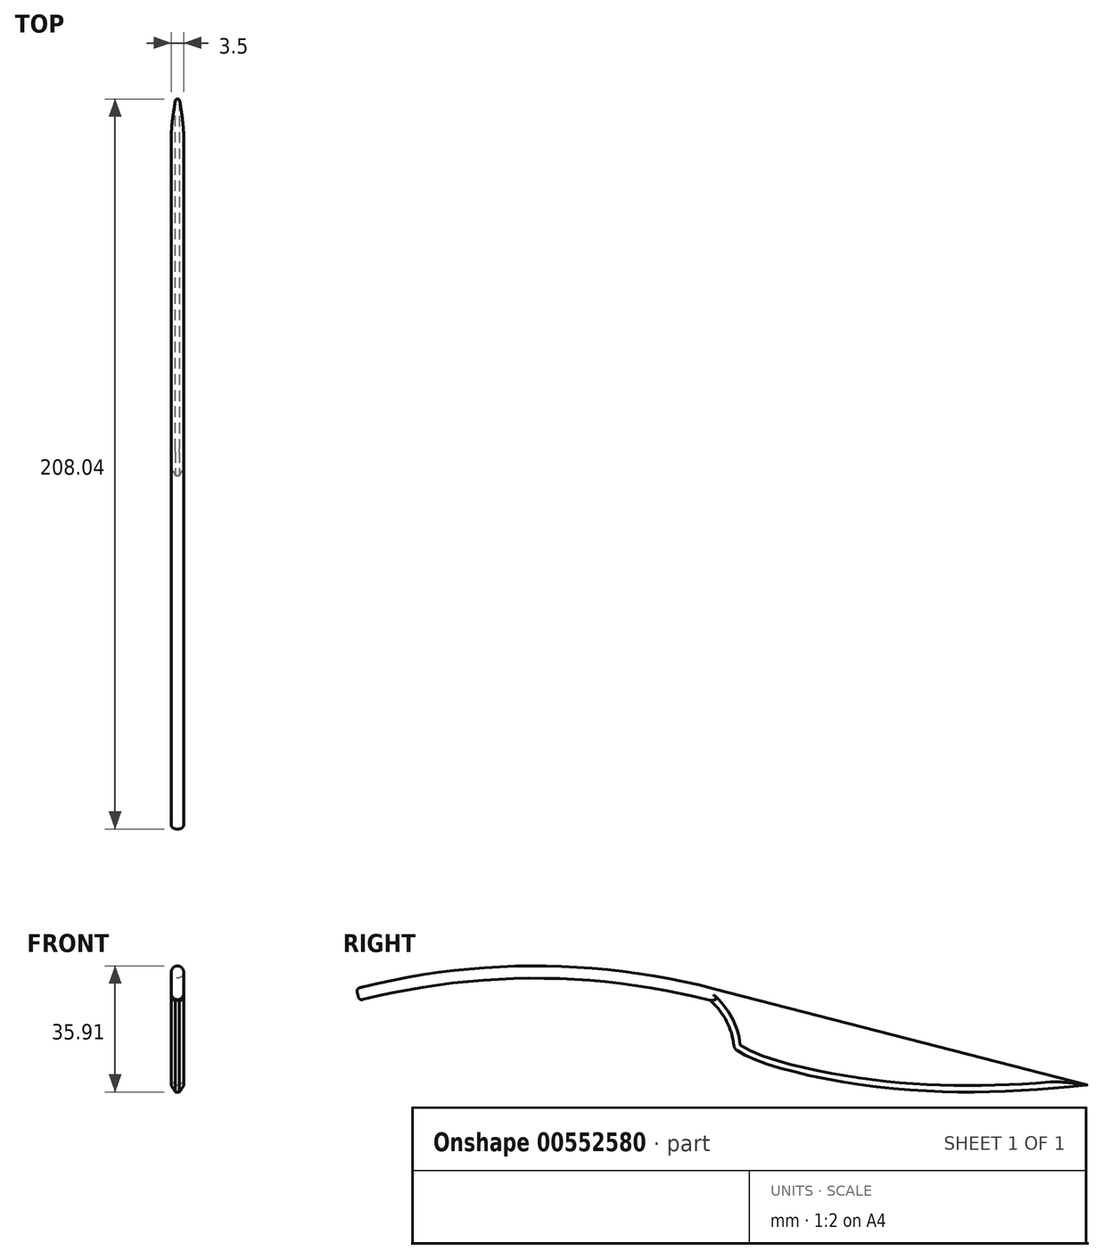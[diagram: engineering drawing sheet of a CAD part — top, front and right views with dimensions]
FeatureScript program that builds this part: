
annotation { "Feature Type Name" : "Feature", "Feature Type Description" : "" }
export const myFeature = defineFeature(function(context is Context, id is Id, definition is map)
    precondition{}
    {
        {
            var Q0;
            Q0=qCreatedBy(makeId("Right.planeOp"),FACE);
            var sketch = newSketch(context, id + "F0", { "sketchPlane" : qUnion([Q0])});
            skLineSegment(sketch, "E0", {"start": v(0, 0) * mm, "end": v(-100, 0) * mm, "construction": true});
            skArc(sketch, "E1", {"start": v(0, 0) * mm, "mid": v(-50, 6.35) * mm, "end": v(-100, 0) * mm, "construction": true});
            skArc(sketch, "E2.0", {"start": v(0.88, 3.39) * mm, "mid": v(-50, 9.85) * mm, "end": v(-100.88, 3.39) * mm, "construction": true});
            skArc(sketch, "E3.0", {"start": v(0.44, 1.7) * mm, "mid": v(-50, 8.1) * mm, "end": v(-100.44, 1.7) * mm});
            skLineSegment(sketch, "E4", {"start": v(-100, 0) * mm, "end": v(-100.88, 3.39) * mm, "construction": true});
            skLineSegment(sketch, "E5", {"start": v(0.88, 3.39) * mm, "end": v(107.38, -24.11) * mm});
            skLineSegment(sketch, "E6", {"start": v(0, 0) * mm, "end": v(106.5, -27.5) * mm, "construction": true});
            skLineSegment(sketch, "E7", {"start": v(0.88, 3.39) * mm, "end": v(0, 0) * mm});
            skLineSegment(sketch, "E8", {"start": v(54.13, -10.36) * mm, "end": v(50.38, -24.88) * mm, "construction": true});
            skLineSegment(sketch, "E9", {"start": v(0, 0) * mm, "end": v(118.47, 0) * mm, "construction": true});
            skArc(sketch, "E10", {"start": v(6.73, -12.78) * mm, "mid": v(4.56, -5.76) * mm, "end": v(0, 0) * mm});
            skLineSegment(sketch, "E11", {"start": v(50.38, -24.88) * mm, "end": v(1.97, -12.38) * mm, "construction": true});
            skFitSpline(sketch, "E12", {"points": [v(6.8, -13.63) * mm, v(50.38, -24.88) * mm, v(107.38, -24.11) * mm], "startDerivative": vector(40.37, -31.88) * mm, "endDerivative": vector(112.17, 10.51) * mm});
            skArc(sketch, "E13.filletArc", {"start": v(6.73, -12.78) * mm, "mid": v(7, -13.59) * mm, "end": v(7.6, -14.2) * mm});
            skPoint(sketch, "E14", {"position": v(26.17, -18.63) * mm});
            skLineSegment(sketch, "E15", {"start": v(0.44, 1.7) * mm, "end": v(97.34, -23.33) * mm});
            skLineSegment(sketch, "E16", {"start": v(97.78, -21.63) * mm, "end": v(96.9, -25.02) * mm, "construction": true});
            skPoint(sketch, "E17", {"position": v(97.34, -23.33) * mm});
            skLineSegment(sketch, "E18", {"start": v(97.34, -23.33) * mm, "end": v(97.78, -21.63) * mm});
            skSolve(sketch);
        }
        {
            var Q0;
            Q0=sQuery(id+"F0.wireOp",EDGE,"E4");
            cPlane(context, id + "F1", {"entities" : qUnion([Q0]), "cplaneType" : CPlaneType.LINE_ANGLE, "offset" : 25 * mm, "angle" : 90 * degree, "width" : 150 * mm, "height" : 150 * mm});
        }
        {
            var Q0;
            Q0=qCreatedBy(id+"F1.planeOp",FACE);
            var sketch = newSketch(context, id + "F2", { "sketchPlane" : qUnion([Q0])});
            skCircle(sketch, "E19", {"center": v(0, 26.75) * mm, "radius": 1.75 * mm});
            skSolve(sketch);
        }
        {
            var Q0;
            Q0=makeQuery(id+"F2.imprint","IMPRINT",FACE,{"disambiguationData":[TD([[makeQuery(id+"F2.imprint","IMPRINT",EDGE,{"derivedFrom":sQuery(id+"F2.wireOp",EDGE,"E19")}),1.0]])]});
            var Q1;
            Q1=sQuery(id+"F0.wireOp",EDGE,"E15");
            var Q2;
            Q2=sQuery(id+"F0.wireOp",EDGE,"E3.0");
            sweep(context, id + "F3", {"profiles" : qUnion([Q0]), "path" : qUnion([Q1, Q2])});
        }
        {
            var Q0;
            {var subQ3=sQuery(id+"F0.wireOp",EDGE,"E10");Q0=makeQuery(id+"F0.imprint","IMPRINT",FACE,{"disambiguationData":[TD([[makeQuery(id+"F0.imprint","IMPRINT",EDGE,{"derivedFrom":subQ3}),-1.0]])]});}
            extrude(context, id + "F4", {"entities" : qUnion([Q0]), "operationType" : NewBodyOperationType.ADD, "depth" : 3.5 * mm, "offsetDistance" : 25 * mm, "symmetric" : true});
        }
        {
            var Q0;
            Q0=makeQuery(id+"F4.opExtrude","CAP_EDGE",EDGE,{"disambiguationData":[OSD([sQuery(id+"F0.wireOp",EDGE,"E12")])],"isStart":false});
            var Q1;
            Q1=makeQuery(id+"F4.opExtrude","CAP_EDGE",EDGE,{"disambiguationData":[OSD([sQuery(id+"F0.wireOp",EDGE,"E12")])],"isStart":true});
            chamfer(context, id + "F5", {"entities" : qUnion([Q0, Q1]), "chamferType" : ChamferType.TWO_OFFSETS, "width1" : 1.8 * mm, "oppositeDirection" : false, "width2" : (3.5 / 3) * mm, "tangentPropagation" : true});
        }
        {
            var Q0;
            {var subQ0=sQuery(id+"F0.wireOp",EDGE,"E15");var subQ1=sQuery(id+"F0.wireOp",EDGE,"E18");var subQ2=sQuery(id+"F0.wireOp",EDGE,"E5");var subQ3=makeQuery(id+"F4.opExtrude","SWEPT_FACE",FACE,{"disambiguationData":[OSD([subQ1])]});Q0=makeQuery(id+"F4.boolean.opBoolean","SPLIT",FACE,{"disambiguationData":[TD([makeQuery(id+"F4.opExtrude","CAP_FACE",FACE,{"disambiguationData":[OSD([subQ2,sQuery(id+"F0.wireOp",EDGE,"E7"),sQuery(id+"F0.wireOp",EDGE,"E10"),sQuery(id+"F0.wireOp",EDGE,"E12"),sQuery(id+"F0.wireOp",EDGE,"E13.filletArc"),subQ0,subQ1])],"isStart":false})])],"derivedFrom":subQ3});}
            var Q1;
            {var subQ0=sQuery(id+"F0.wireOp",EDGE,"E15");var subQ1=sQuery(id+"F0.wireOp",EDGE,"E5");var subQ2=sQuery(id+"F0.wireOp",EDGE,"E18");var subQ3=makeQuery(id+"F4.opExtrude","SWEPT_FACE",FACE,{"disambiguationData":[OSD([subQ2])]});Q1=makeQuery(id+"F4.boolean.opBoolean","SPLIT",FACE,{"disambiguationData":[TD([makeQuery(id+"F4.opExtrude","CAP_FACE",FACE,{"disambiguationData":[OSD([subQ1,sQuery(id+"F0.wireOp",EDGE,"E7"),sQuery(id+"F0.wireOp",EDGE,"E10"),sQuery(id+"F0.wireOp",EDGE,"E12"),sQuery(id+"F0.wireOp",EDGE,"E13.filletArc"),subQ0,subQ2])],"isStart":true})])],"derivedFrom":subQ3});}
            extrude(context, id + "F6", {"entities" : qUnion([Q0, Q1]), "operationType" : NewBodyOperationType.REMOVE, "oppositeDirection" : true, "depth" : 25 * mm, "offsetDistance" : 25 * mm});
        }
        {
            var Q0;
            Q0=makeQuery(id+"F3.opSweep","CAP_EDGE",EDGE,{"disambiguationData":[OSD([sQuery(id+"F0.wireOp",VERTEX,"E3.0.end"),sQuery(id+"F2.wireOp",EDGE,"E19")])],"isStart":true});
            fillet(context, id + "F7", {"entities" : qUnion([Q0]), "radius" : 1 * mm, "tangentPropagation" : true, "allowEdgeOverflow" : false});
        }
        {
            var Q0;
            {var subQ0=sQuery(id+"F0.wireOp",EDGE,"E7");var subQ1=makeQuery(id+"F4.opExtrude","SWEPT_FACE",FACE,{"disambiguationData":[OSD([subQ0])]});var subQ3=sQuery(id+"F0.wireOp",EDGE,"E15");var subQ4=sQuery(id+"F0.wireOp",EDGE,"E10");Q0=makeQuery(id+"F5.opChamfer","BLEND_EDGE",EDGE,{"blendedFrom":[makeQuery(id+"F4.opExtrude","CAP_EDGE",EDGE,{"disambiguationData":[OSD([subQ4])],"isStart":true}),makeQuery(id+"F4.boolean.opBoolean","SPLIT",FACE,{"disambiguationData":[TD([makeQuery(id+"F4.opExtrude","CAP_FACE",FACE,{"disambiguationData":[OSD([sQuery(id+"F0.wireOp",EDGE,"E5"),subQ0,subQ4,sQuery(id+"F0.wireOp",EDGE,"E12"),sQuery(id+"F0.wireOp",EDGE,"E13.filletArc"),subQ3,sQuery(id+"F0.wireOp",EDGE,"E18")])],"isStart":true})])],"derivedFrom":subQ1})],"blendedInto":[makeQuery(id+"F4.boolean.opBoolean","SPLIT",FACE,{"disambiguationData":[TD([makeQuery(id+"F4.opExtrude","CAP_FACE",FACE,{"disambiguationData":[OSD([sQuery(id+"F0.wireOp",EDGE,"E5"),subQ0,subQ4,sQuery(id+"F0.wireOp",EDGE,"E12"),sQuery(id+"F0.wireOp",EDGE,"E13.filletArc"),subQ3,sQuery(id+"F0.wireOp",EDGE,"E18")])],"isStart":true})])],"derivedFrom":subQ1})]});}
            fillet(context, id + "F8", {"entities" : qUnion([Q0]), "radius" : 0.6 * mm, "tangentPropagation" : true, "allowEdgeOverflow" : false});
        }
        {
            var Q0;
            {var subQ0=sQuery(id+"F0.wireOp",EDGE,"E7");var subQ1=makeQuery(id+"F4.opExtrude","SWEPT_FACE",FACE,{"disambiguationData":[OSD([subQ0])]});var subQ2=sQuery(id+"F0.wireOp",EDGE,"E15");var subQ3=sQuery(id+"F0.wireOp",EDGE,"E10");Q0=makeQuery(id+"F5.opChamfer","BLEND_EDGE",EDGE,{"blendedFrom":[makeQuery(id+"F4.opExtrude","CAP_EDGE",EDGE,{"disambiguationData":[OSD([subQ3])],"isStart":false}),makeQuery(id+"F4.boolean.opBoolean","SPLIT",FACE,{"disambiguationData":[TD([makeQuery(id+"F4.opExtrude","CAP_FACE",FACE,{"disambiguationData":[OSD([sQuery(id+"F0.wireOp",EDGE,"E5"),subQ0,subQ3,sQuery(id+"F0.wireOp",EDGE,"E12"),sQuery(id+"F0.wireOp",EDGE,"E13.filletArc"),subQ2,sQuery(id+"F0.wireOp",EDGE,"E18")])],"isStart":false})])],"derivedFrom":subQ1})],"blendedInto":[makeQuery(id+"F4.boolean.opBoolean","SPLIT",FACE,{"disambiguationData":[TD([makeQuery(id+"F4.opExtrude","CAP_FACE",FACE,{"disambiguationData":[OSD([sQuery(id+"F0.wireOp",EDGE,"E5"),subQ0,subQ3,sQuery(id+"F0.wireOp",EDGE,"E12"),sQuery(id+"F0.wireOp",EDGE,"E13.filletArc"),subQ2,sQuery(id+"F0.wireOp",EDGE,"E18")])],"isStart":false})])],"derivedFrom":subQ1})]});}
            fillet(context, id + "F9", {"entities" : qUnion([Q0]), "radius" : 0.6 * mm, "tangentPropagation" : true, "allowEdgeOverflow" : false});
        }
    });
